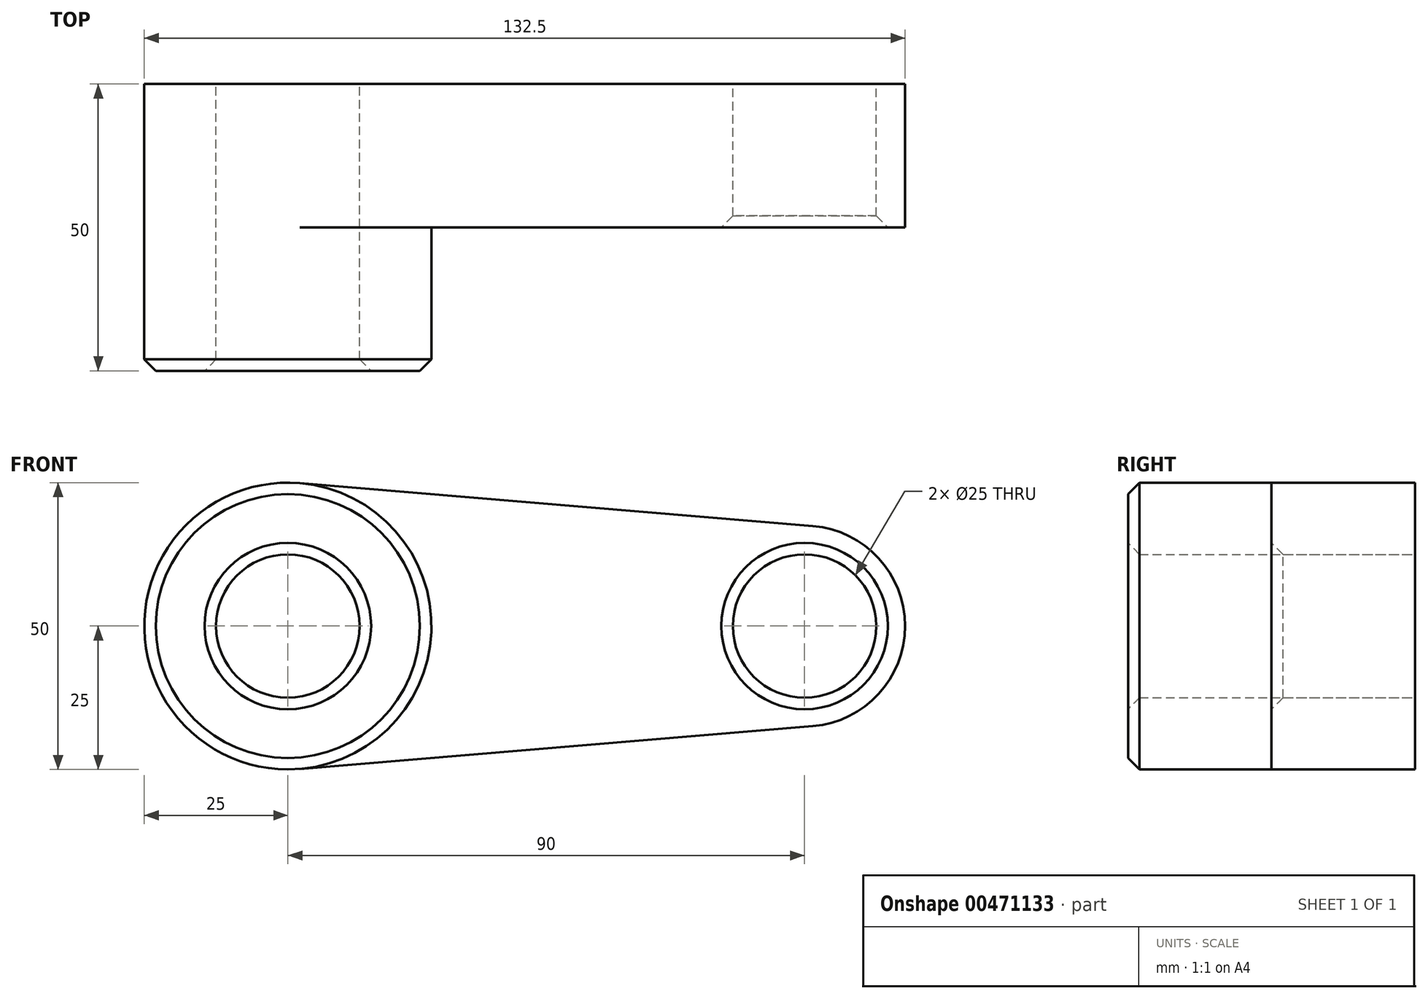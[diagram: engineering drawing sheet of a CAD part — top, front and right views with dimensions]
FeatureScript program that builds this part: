
annotation { "Feature Type Name" : "Feature", "Feature Type Description" : "" }
export const myFeature = defineFeature(function(context is Context, id is Id, definition is map)
    precondition{}
    {
        {
            var Q0;
            Q0=qCreatedBy(makeId("Front.planeOp"),FACE);
            var sketch = newSketch(context, id + "F0", { "sketchPlane" : qUnion([Q0])});
            skCircle(sketch, "E0", {"center": v(0, 0) * mm, "radius": 25 * mm});
            skCircle(sketch, "E1", {"center": v(90, 0) * mm, "radius": 17.5 * mm});
            skLineSegment(sketch, "E2", {"start": v(2.08, 24.91) * mm, "end": v(91.46, 17.44) * mm});
            skLineSegment(sketch, "E3", {"start": v(2.08, -24.91) * mm, "end": v(91.46, -17.44) * mm});
            skCircle(sketch, "E4", {"center": v(0, 0) * mm, "radius": 12.5 * mm});
            skCircle(sketch, "E5", {"center": v(90, 0) * mm, "radius": 12.5 * mm});
            skSolve(sketch);
        }
        {
            var Q0;
            Q0 = qSketchRegion(id + "F0", true);
            extrude(context, id + "F1", {"entities" : qUnion([Q0]), "depth" : 25 * mm});
        }
        {
            var Q0;
            Q0=makeQuery(id+"F0.imprint","IMPRINT",FACE,{"disambiguationData":[TD([[makeQuery(id+"F0.imprint","IMPRINT",EDGE,{"derivedFrom":sQuery(id+"F0.wireOp",EDGE,"E4")}),-1.0]])]});
            extrude(context, id + "F2", {"entities" : qUnion([Q0]), "operationType" : NewBodyOperationType.ADD, "depth" : 50 * mm});
        }
        {
            var Q0;
            Q0=makeQuery(id+"F2.opExtrude","CAP_EDGE",EDGE,{"disambiguationData":[OSD([sQuery(id+"F0.wireOp",EDGE,"E0")])],"isStart":false});
            var Q1;
            Q1=makeQuery(id+"F2.opExtrude","CAP_EDGE",EDGE,{"disambiguationData":[OSD([sQuery(id+"F0.wireOp",EDGE,"E4")])],"isStart":false});
            var Q2;
            Q2=makeQuery(id+"F1.opExtrude","CAP_EDGE",EDGE,{"disambiguationData":[OSD([sQuery(id+"F0.wireOp",EDGE,"E5")])],"isStart":false});
            chamfer(context, id + "F3", {"entities" : qUnion([Q0, Q1, Q2]), "width" : 2 * mm, "tangentPropagation" : true});
        }
    });
